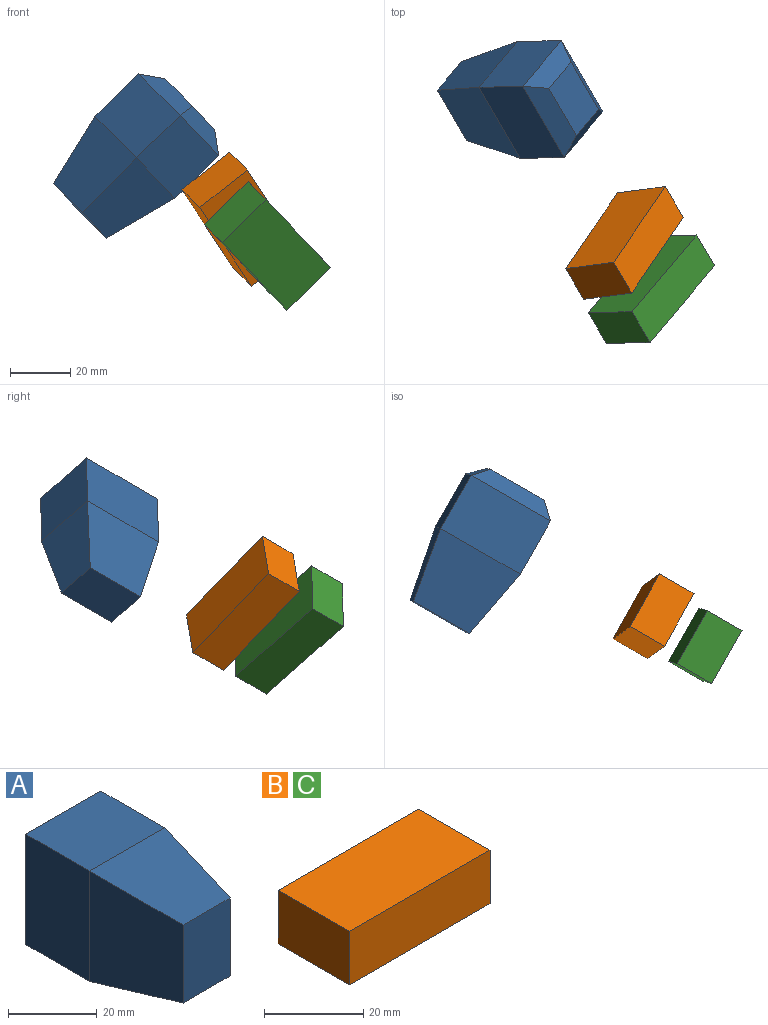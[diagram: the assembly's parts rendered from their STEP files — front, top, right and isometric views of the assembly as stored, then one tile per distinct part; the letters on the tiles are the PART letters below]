
ASSEMBLY  parts=3 mates=2
PART A: 14 faces, bbox 23.9x50.8x30.5 mm
  f0: plane 30.49x25.4mm, normal (-0.98,-0.17,0), area 671mm2, adj f1,f3,f4,f9
  f1: plane 25.4x23.94mm, normal (0,-0.17,-0.98), area 502mm2, adj f0,f2,f4,f8
  f2: plane 30.49x25.4mm, normal (0.98,-0.17,0), area 671mm2, adj f1,f3,f4,f7
  f3: plane 25.4x23.94mm, normal (0,-0.17,0.98), area 502mm2, adj f0,f2,f4,f6
  f4: plane 21.54x14.99mm, normal (0,-1,0), area 322.7mm2, adj f0,f1,f2,f3
  f5: plane 20.33x13.78mm, normal (0,1,0), area 280.3mm2, adj f10,f11,f12,f13
  f6: plane 23.94x20.32mm, normal (0,0,1), area 486.5mm2, adj f3,f7,f9,f12
  f7: plane 30.49x20.32mm, normal (1,0,0), area 619.6mm2, adj f2,f6,f8,f13
  f8: plane 23.94x20.32mm, normal (0,0,-1), area 486.5mm2, adj f1,f7,f9,f11
  f9: plane 30.49x20.32mm, normal (-1,0,0), area 619.6mm2, adj f0,f6,f8,f10
  f10: plane 30.49x5.08mm, normal (-0.71,0.71,0), area 182.6mm2, adj f5,f9,f11,f12
  f11: plane 23.94x5.08mm, normal (0,0.71,-0.71), area 135.5mm2, adj f5,f8,f10,f13
  f12: plane 23.94x5.08mm, normal (0,0.71,0.71), area 135.5mm2, adj f5,f6,f10,f13
  f13: plane 30.49x5.08mm, normal (0.71,0.71,0), area 182.6mm2, adj f5,f7,f11,f12
PART B: 6 faces, bbox 40.1x20.3x13.2 mm
  f0: plane 40.13x13.21mm, normal (0,1,0), area 530mm2, adj f1,f3,f4,f5
  f1: plane 20.27x13.21mm, normal (-1,0,0), area 267.8mm2, adj f0,f2,f4,f5
  f2: plane 40.13x13.21mm, normal (0,-1,0), area 530mm2, adj f1,f3,f4,f5
  f3: plane 20.27x13.21mm, normal (1,0,0), area 267.8mm2, adj f0,f2,f4,f5
  f4: plane 40.13x20.27mm, normal (0,0,1), area 813.4mm2, adj f0,f1,f2,f3
  f5: plane 40.13x20.27mm, normal (0,0,-1), area 813.4mm2, adj f0,f1,f2,f3
PART C: same geometry as B
PLACE A rot(axis=(0.82,0.57,-0.05),116.8deg) t=(85.1,82.21,-50.11)mm
PLACE B rot(axis=(0.53,-0.67,0.52),171.4deg) t=(75.81,39.07,-10.61)mm
PLACE C rot(axis=(0.82,0.57,-0.05),116.8deg) t=(70.76,24.17,-34.29)mm
MATE slider A.f6 <-> C.f5  axis (0.45,-0.77,-0.45) through (50.49,69.49,0.15)mm
MATE cylindrical C.f4 <-> B.f5  axis (0.45,-0.77,-0.45) through (83.3,13.31,-32.43)mm
